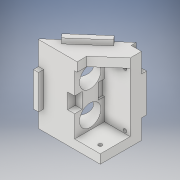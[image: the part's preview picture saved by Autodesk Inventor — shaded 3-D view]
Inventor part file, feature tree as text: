
AUTODESK INVENTOR PART (.ipt)
format: ipt  version: 2019 (Build 230136000, 136)  size: 286,720 bytes
history: native  units: mm
features: sketch x15, extrude x13, projected_geometry x3, hole x2, other x1
ambient origin geometry x8: Origin, YZ Plane, XZ Plane, XY Plane, X Axis, Y Axis, Z Axis, Center Point
bodies: Body1 (feature_tree)
feature tree (34):
  other  "Твердое тело1"
  extrude  "Выдавливание1"  Depth=35.0mm
  extrude  "Выдавливание2"  Depth=40.0mm
  extrude  "Выдавливание3"  Depth=30.0mm
  extrude  "Выдавливание4"  Depth=4.0mm
  extrude  "Выдавливание5"  Depth=22.25mm
  extrude  "Выдавливание6"  Depth=60.0mm TaperAngle=0.0deg
  extrude  "Выдавливание7"  Depth=46.0mm
  extrude  "Выдавливание8"  Depth=2.0mm TaperAngle=0.0deg
  extrude  "Выдавливание9"  Depth=16.6mm
  extrude  "Выдавливание10"  Depth=26.0mm
  extrude  "Выдавливание11"  Depth=2.0mm TaperAngle=0.0deg
  extrude  "Выдавливание12"  Depth=5.0mm
  extrude  "Выдавливание15"  Depth=12.0mm
  hole  "Отверстие1"  [1 undecoded]
  hole  "Отверстие2"  [1 undecoded]
  sketch  "Эскиз1"
  sketch  "Эскиз2"
  sketch  "Эскиз3"
  sketch  "Эскиз4"
  sketch  "Эскиз5"
  sketch  "Эскиз6"
  sketch  "Эскиз7"
  sketch  "Эскиз8"
  projected_geometry  "Спроецированная петля1"
  sketch  "Эскиз9"
  projected_geometry  "Спроецированная петля2"
  sketch  "Эскиз10"
  projected_geometry  "Спроецированная петля3"
  sketch  "Эскиз12"
  sketch  "Эскиз13"
  sketch  "Эскиз16"
  sketch  "Эскиз17"
  sketch  "Эскиз19"
note: 2 required parameter values undecoded (feature->parameter linkage not recoverable at this tier; creation-order binding heuristic only, values carry confidence <= 0.55)
